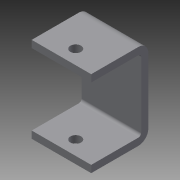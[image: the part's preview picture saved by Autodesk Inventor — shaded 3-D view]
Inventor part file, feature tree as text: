
AUTODESK INVENTOR PART (.ipt)
format: ipt  version: 2013 (Build 170138000, 138)  size: 114,688 bytes
history: native  units: in
note: dims shown in document units (in); Inventor stores cm internally (conversion verified against a paired STEP export)
features: sheet_metal_op x4, sketch x3, other x2, extrude x1
ambient origin geometry x8: Origin, YZ Plane, XZ Plane, XY Plane, X Axis, Y Axis, Z Axis, Center Point
bodies: Solid1 (feature_tree)
feature tree (10):
  sheet_metal_op  "Face1"
  sheet_metal_op  "Flange1"
  extrude  "Extrusion1"  Depth=1.15in
  sketch  "Sketch1"  dims[d4=0.5788in d5=1.15in]
  other  "Plate1"
  sketch  "Sketch2"  dims[d6=0.125in]
  other  "Plate2"
  sheet_metal_op  "Bend1"
  sheet_metal_op  "Corner1"
  sketch  "Sketch3"  dims[d7=0.125in d8=0.0625in d9=0.25in d10=0.125in d11=1.0in d12=90.0deg d13=0.05in d14=0.5in d15=0.125in d16=0.125in d17=0.25in d18=0.1875in d19=2999.0in d20=0.0in d21=0.575in]
